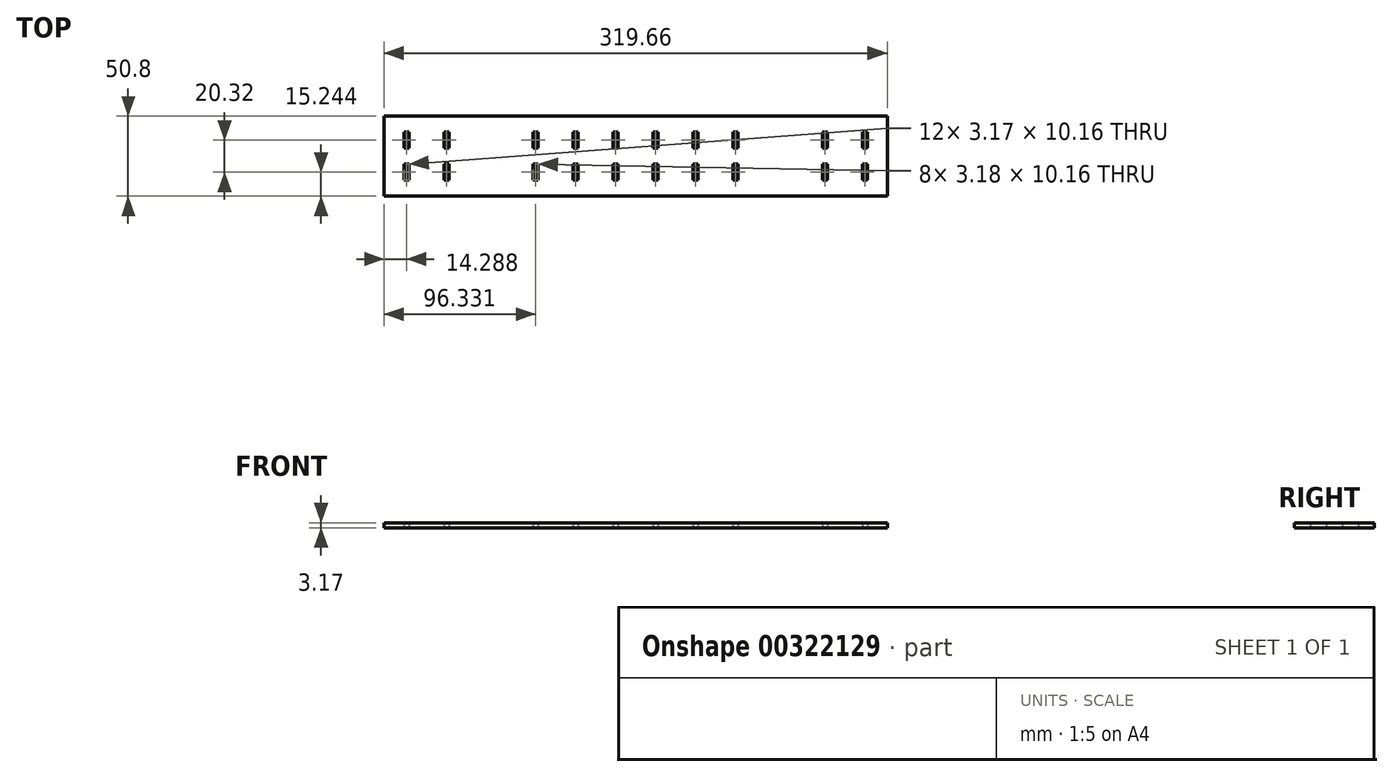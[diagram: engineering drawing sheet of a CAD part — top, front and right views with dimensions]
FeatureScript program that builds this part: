
annotation { "Feature Type Name" : "Feature", "Feature Type Description" : "" }
export const myFeature = defineFeature(function(context is Context, id is Id, definition is map)
    precondition{}
    {
        {
            var Q0;
            Q0=qCreatedBy(makeId("Top.planeOp"),FACE);
            var sketch = newSketch(context, id + "F0", { "sketchPlane" : qUnion([Q0])});
            skLineSegment(sketch, "E0.left", {"start": v(190.5, -28.18) * mm, "end": v(190.5, 22.62) * mm});
            skLineSegment(sketch, "E0.right", {"start": v(-129.16, -28.18) * mm, "end": v(-129.16, 22.62) * mm});
            skPoint(sketch, "E0.middle", {"position": v(0, 0) * mm});
            skLineSegment(sketch, "E1.bottom", {"start": v(177.8, 22.62) * mm, "end": v(174.63, 22.62) * mm});
            skLineSegment(sketch, "E2.0.1.0", {"start": v(177.8, 12.46) * mm, "end": v(174.63, 12.46) * mm});
            skLineSegment(sketch, "E2.0.1.1", {"start": v(177.8, 2.3) * mm, "end": v(174.63, 2.3) * mm});
            skLineSegment(sketch, "E2.0.1.2", {"start": v(177.8, 2.3) * mm, "end": v(177.8, 12.46) * mm});
            skPoint(sketch, "E2.0.1.3", {"position": v(176.21, 7.38) * mm});
            skLineSegment(sketch, "E2.0.1.4", {"start": v(174.63, 2.3) * mm, "end": v(174.63, 12.46) * mm});
            skLineSegment(sketch, "E2.0.2.0", {"start": v(177.8, -7.86) * mm, "end": v(174.63, -7.86) * mm});
            skLineSegment(sketch, "E2.0.2.1", {"start": v(177.8, -18.02) * mm, "end": v(174.63, -18.02) * mm});
            skLineSegment(sketch, "E2.0.2.2", {"start": v(177.8, -18.02) * mm, "end": v(177.8, -7.86) * mm});
            skPoint(sketch, "E2.0.2.3", {"position": v(176.21, -12.94) * mm});
            skLineSegment(sketch, "E2.0.2.4", {"start": v(174.63, -18.02) * mm, "end": v(174.63, -7.86) * mm});
            skLineSegment(sketch, "E2.1.0.1", {"start": v(152.4, 22.62) * mm, "end": v(149.23, 22.62) * mm});
            skLineSegment(sketch, "E2.1.1.0", {"start": v(152.4, 12.46) * mm, "end": v(149.23, 12.46) * mm});
            skLineSegment(sketch, "E2.1.1.1", {"start": v(152.4, 2.3) * mm, "end": v(149.23, 2.3) * mm});
            skLineSegment(sketch, "E2.1.1.2", {"start": v(152.4, 2.3) * mm, "end": v(152.4, 12.46) * mm});
            skPoint(sketch, "E2.1.1.3", {"position": v(150.81, 7.38) * mm});
            skLineSegment(sketch, "E2.1.1.4", {"start": v(149.23, 2.3) * mm, "end": v(149.23, 12.46) * mm});
            skLineSegment(sketch, "E2.1.2.0", {"start": v(152.4, -7.86) * mm, "end": v(149.23, -7.86) * mm});
            skLineSegment(sketch, "E2.1.2.1", {"start": v(152.4, -18.02) * mm, "end": v(149.23, -18.02) * mm});
            skLineSegment(sketch, "E2.1.2.2", {"start": v(152.4, -18.02) * mm, "end": v(152.4, -7.86) * mm});
            skPoint(sketch, "E2.1.2.3", {"position": v(150.81, -12.94) * mm});
            skLineSegment(sketch, "E2.1.2.4", {"start": v(149.23, -18.02) * mm, "end": v(149.23, -7.86) * mm});
            skLineSegment(sketch, "E2.direction1", {"start": v(174.63, 22.62) * mm, "end": v(149.23, 22.62) * mm, "construction": true});
            skLineSegment(sketch, "E2.direction2", {"start": v(174.63, 22.62) * mm, "end": v(174.63, 2.3) * mm, "construction": true});
            skLineSegment(sketch, "E3", {"start": v(190.5, -28.18) * mm, "end": v(-129.16, -28.18) * mm});
            skLineSegment(sketch, "E4", {"start": v(-129.16, 22.62) * mm, "end": v(190.5, 22.62) * mm});
            skPoint(sketch, "E5.orphan", {"position": v(190.5, 50.56) * mm});
            skPoint(sketch, "E0.bottom.start.orphan", {"position": v(190.5, -50.56) * mm});
            skPoint(sketch, "E6.orphan", {"position": v(-129.16, 50.56) * mm});
            skPoint(sketch, "E7.orphan", {"position": v(-129.16, -50.56) * mm});
            skLineSegment(sketch, "E8.bottom", {"start": v(92.58, 12.46) * mm, "end": v(95.76, 12.46) * mm});
            skLineSegment(sketch, "E8.top", {"start": v(92.58, 2.3) * mm, "end": v(95.76, 2.3) * mm});
            skLineSegment(sketch, "E8.left", {"start": v(92.58, 12.46) * mm, "end": v(92.58, 2.3) * mm});
            skLineSegment(sketch, "E8.right", {"start": v(95.76, 12.46) * mm, "end": v(95.76, 2.3) * mm});
            skLineSegment(sketch, "E9.0.1.0", {"start": v(95.76, -7.86) * mm, "end": v(95.76, -18.02) * mm});
            skLineSegment(sketch, "E9.0.1.1", {"start": v(92.58, -7.86) * mm, "end": v(95.76, -7.86) * mm});
            skLineSegment(sketch, "E9.0.1.2", {"start": v(92.58, -7.86) * mm, "end": v(92.58, -18.02) * mm});
            skLineSegment(sketch, "E9.0.1.3", {"start": v(92.58, -18.02) * mm, "end": v(95.76, -18.02) * mm});
            skLineSegment(sketch, "E9.1.0.0", {"start": v(70.36, 12.46) * mm, "end": v(70.36, 2.3) * mm});
            skLineSegment(sketch, "E9.1.0.1", {"start": v(67.18, 12.46) * mm, "end": v(70.36, 12.46) * mm});
            skLineSegment(sketch, "E9.1.0.2", {"start": v(67.18, 12.46) * mm, "end": v(67.18, 2.3) * mm});
            skLineSegment(sketch, "E9.1.0.3", {"start": v(67.18, 2.3) * mm, "end": v(70.36, 2.3) * mm});
            skLineSegment(sketch, "E9.1.1.0", {"start": v(70.36, -7.86) * mm, "end": v(70.36, -18.02) * mm});
            skLineSegment(sketch, "E9.1.1.1", {"start": v(67.18, -7.86) * mm, "end": v(70.36, -7.86) * mm});
            skLineSegment(sketch, "E9.1.1.2", {"start": v(67.18, -7.86) * mm, "end": v(67.18, -18.02) * mm});
            skLineSegment(sketch, "E9.1.1.3", {"start": v(67.18, -18.02) * mm, "end": v(70.36, -18.02) * mm});
            skLineSegment(sketch, "E9.2.0.0", {"start": v(44.96, 12.46) * mm, "end": v(44.96, 2.3) * mm});
            skLineSegment(sketch, "E9.2.0.1", {"start": v(41.78, 12.46) * mm, "end": v(44.96, 12.46) * mm});
            skLineSegment(sketch, "E9.2.0.2", {"start": v(41.78, 12.46) * mm, "end": v(41.78, 2.3) * mm});
            skLineSegment(sketch, "E9.2.0.3", {"start": v(41.78, 2.3) * mm, "end": v(44.96, 2.3) * mm});
            skLineSegment(sketch, "E9.2.1.0", {"start": v(44.96, -7.86) * mm, "end": v(44.96, -18.02) * mm});
            skLineSegment(sketch, "E9.2.1.1", {"start": v(41.78, -7.86) * mm, "end": v(44.96, -7.86) * mm});
            skLineSegment(sketch, "E9.2.1.2", {"start": v(41.78, -7.86) * mm, "end": v(41.78, -18.02) * mm});
            skLineSegment(sketch, "E9.2.1.3", {"start": v(41.78, -18.02) * mm, "end": v(44.96, -18.02) * mm});
            skLineSegment(sketch, "E9.direction1", {"start": v(92.58, 2.3) * mm, "end": v(67.18, 2.3) * mm, "construction": true});
            skLineSegment(sketch, "E9.direction2", {"start": v(92.58, 2.3) * mm, "end": v(92.58, -18.02) * mm, "construction": true});
            skLineSegment(sketch, "E10", {"start": v(30.67, 22.62) * mm, "end": v(30.67, -28.18) * mm, "construction": true});
            skLineSegment(sketch, "E11.MirrorCS", {"start": v(-31.24, 2.3) * mm, "end": v(-34.42, 2.3) * mm});
            skLineSegment(sketch, "E12.MirrorCS", {"start": v(-9.02, 12.46) * mm, "end": v(-9.02, 2.3) * mm});
            skLineSegment(sketch, "E13.MirrorCS", {"start": v(-113.28, 2.3) * mm, "end": v(-113.28, 12.46) * mm});
            skLineSegment(sketch, "E14.MirrorCS", {"start": v(-31.24, -7.86) * mm, "end": v(-34.42, -7.86) * mm});
            skLineSegment(sketch, "E15.MirrorCS", {"start": v(19.56, 12.46) * mm, "end": v(16.38, 12.46) * mm});
            skLineSegment(sketch, "E16.MirrorCS", {"start": v(-31.24, 2.3) * mm, "end": v(-5.84, 2.3) * mm, "construction": true});
            skLineSegment(sketch, "E17.MirrorCS", {"start": v(-91.06, 12.46) * mm, "end": v(-87.88, 12.46) * mm});
            skLineSegment(sketch, "E18.MirrorCS", {"start": v(19.56, -7.86) * mm, "end": v(16.38, -7.86) * mm});
            skLineSegment(sketch, "E19.MirrorCS", {"start": v(-5.84, -7.86) * mm, "end": v(-9.02, -7.86) * mm});
            skLineSegment(sketch, "E20.MirrorCS", {"start": v(-91.06, -18.02) * mm, "end": v(-91.06, -7.86) * mm});
            skLineSegment(sketch, "E21.MirrorCS", {"start": v(-34.42, 12.46) * mm, "end": v(-34.42, 2.3) * mm});
            skLineSegment(sketch, "E22.MirrorCS", {"start": v(-5.84, 12.46) * mm, "end": v(-5.84, 2.3) * mm});
            skLineSegment(sketch, "E23.MirrorCS", {"start": v(-31.24, -18.02) * mm, "end": v(-34.42, -18.02) * mm});
            skPoint(sketch, "E24.MirrorP", {"position": v(-114.87, -12.94) * mm});
            skLineSegment(sketch, "E25.MirrorCS", {"start": v(19.56, 2.3) * mm, "end": v(16.38, 2.3) * mm});
            skLineSegment(sketch, "E26.MirrorCS", {"start": v(19.56, -18.02) * mm, "end": v(16.38, -18.02) * mm});
            skLineSegment(sketch, "E27.MirrorCS", {"start": v(-116.46, -7.86) * mm, "end": v(-113.28, -7.86) * mm});
            skLineSegment(sketch, "E28.MirrorCS", {"start": v(-31.24, 12.46) * mm, "end": v(-34.42, 12.46) * mm});
            skLineSegment(sketch, "E29.MirrorCS", {"start": v(16.38, 12.46) * mm, "end": v(16.38, 2.3) * mm});
            skLineSegment(sketch, "E30.MirrorCS", {"start": v(-9.02, -7.86) * mm, "end": v(-9.02, -18.02) * mm});
            skLineSegment(sketch, "E31.MirrorCS", {"start": v(-116.46, -18.02) * mm, "end": v(-113.28, -18.02) * mm});
            skLineSegment(sketch, "E32.MirrorCS", {"start": v(-91.06, 2.3) * mm, "end": v(-87.88, 2.3) * mm});
            skLineSegment(sketch, "E33.MirrorCS", {"start": v(-91.06, -18.02) * mm, "end": v(-87.88, -18.02) * mm});
            skPoint(sketch, "E34.MirrorP", {"position": v(-89.47, -12.94) * mm});
            skLineSegment(sketch, "E35.MirrorCS", {"start": v(-116.46, 12.46) * mm, "end": v(-113.28, 12.46) * mm});
            skLineSegment(sketch, "E36.MirrorCS", {"start": v(-31.24, 12.46) * mm, "end": v(-31.24, 2.3) * mm});
            skLineSegment(sketch, "E37.MirrorCS", {"start": v(-5.84, 12.46) * mm, "end": v(-9.02, 12.46) * mm});
            skLineSegment(sketch, "E38.MirrorCS", {"start": v(-31.24, -7.86) * mm, "end": v(-31.24, -18.02) * mm});
            skLineSegment(sketch, "E39.MirrorCS", {"start": v(-116.46, -18.02) * mm, "end": v(-116.46, -7.86) * mm});
            skPoint(sketch, "E40.MirrorP", {"position": v(-114.87, 7.38) * mm});
            skLineSegment(sketch, "E41.MirrorCS", {"start": v(-91.06, 2.3) * mm, "end": v(-91.06, 12.46) * mm});
            skLineSegment(sketch, "E42.MirrorCS", {"start": v(19.56, 12.46) * mm, "end": v(19.56, 2.3) * mm});
            skLineSegment(sketch, "E43.MirrorCS", {"start": v(-31.24, 2.3) * mm, "end": v(-31.24, -18.02) * mm, "construction": true});
            skLineSegment(sketch, "E44.MirrorCS", {"start": v(19.56, -7.86) * mm, "end": v(19.56, -18.02) * mm});
            skLineSegment(sketch, "E45.MirrorCS", {"start": v(-116.46, 2.3) * mm, "end": v(-113.28, 2.3) * mm});
            skLineSegment(sketch, "E46.MirrorCS", {"start": v(-5.84, -7.86) * mm, "end": v(-5.84, -18.02) * mm});
            skLineSegment(sketch, "E47.MirrorCS", {"start": v(-113.28, -18.02) * mm, "end": v(-113.28, -7.86) * mm});
            skLineSegment(sketch, "E48.MirrorCS", {"start": v(-87.88, -18.02) * mm, "end": v(-87.88, -7.86) * mm});
            skLineSegment(sketch, "E49.MirrorCS", {"start": v(-5.84, -18.02) * mm, "end": v(-9.02, -18.02) * mm});
            skLineSegment(sketch, "E50.MirrorCS", {"start": v(-87.88, 2.3) * mm, "end": v(-87.88, 12.46) * mm});
            skLineSegment(sketch, "E51.MirrorCS", {"start": v(-116.46, 2.3) * mm, "end": v(-116.46, 12.46) * mm});
            skLineSegment(sketch, "E52.MirrorCS", {"start": v(-34.42, -7.86) * mm, "end": v(-34.42, -18.02) * mm});
            skLineSegment(sketch, "E53.MirrorCS", {"start": v(-5.84, 2.3) * mm, "end": v(-9.02, 2.3) * mm});
            skPoint(sketch, "E54.MirrorP", {"position": v(-89.47, 7.38) * mm});
            skLineSegment(sketch, "E55.MirrorCS", {"start": v(-91.06, -7.86) * mm, "end": v(-87.88, -7.86) * mm});
            skLineSegment(sketch, "E56.MirrorCS", {"start": v(16.38, -7.86) * mm, "end": v(16.38, -18.02) * mm});
            skSolve(sketch);
        }
        {
            var Q0;
            Q0=makeQuery(id+"F0.imprint","IMPRINT",FACE,{"disambiguationData":[TD([[makeQuery(id+"F0.imprint","IMPRINT",EDGE,{"derivedFrom":sQuery(id+"F0.wireOp",EDGE,"E2.0.1.0")}),-1.0]])]});
            extrude(context, id + "F1", {"entities" : qUnion([Q0]), "depth" : 3.17 * mm});
        }
    });
